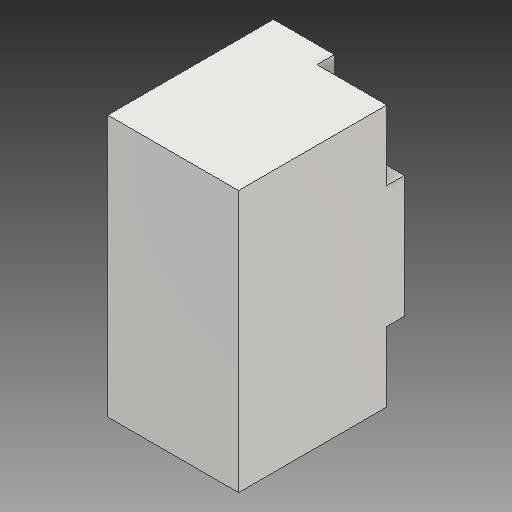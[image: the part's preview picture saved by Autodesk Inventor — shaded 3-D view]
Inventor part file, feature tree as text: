
AUTODESK INVENTOR PART (.ipt)
format: ipt  version: 2018 (Build 220112000, 112)  size: 136,704 bytes
history: native  units: mm
features: extrude x3, sketch x3, projected_geometry x3
ambient origin geometry x8: Origin, YZ Plane, XZ Plane, XY Plane, X Axis, Y Axis, Z Axis, Center Point
bodies: Volumenkörper1 (feature_tree)
feature tree (9):
  extrude  "Extrusion1"  Depth=150.0mm
  extrude  "Extrusion2"  Depth=80.0mm
  extrude  "Extrusion3"  Depth=80.0mm
  sketch  "Skizze1"  dims[d0=300.0mm d1=150.0mm]
  sketch  "Skizze2"  dims[d2=190.0mm d3=0.0mm d4=80.0mm]
  projected_geometry  "Projizierte Kontur1"
  sketch  "Skizze3"  dims[d5=80.0mm d6=80.0mm d7=80.0mm d8=20.0mm d9=20.0mm d10=20.0mm d11=0.0mm d12=15.0mm d13=15.0mm d14=20.0mm d15=0.0mm d16=40.0mm d17=40.0mm d18=40.0mm d19=40.0mm]
  projected_geometry  "Projizierte Kontur2"
  projected_geometry  "Projizierte Kontur3"
